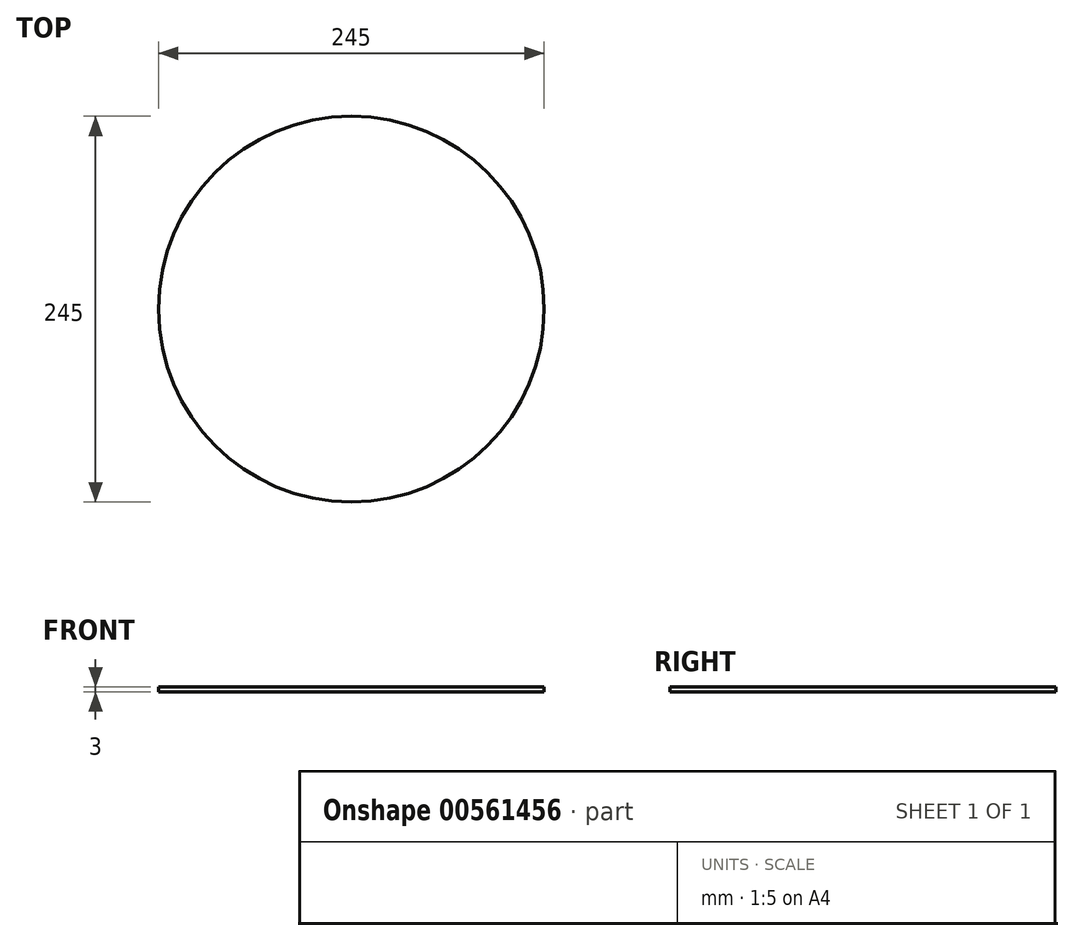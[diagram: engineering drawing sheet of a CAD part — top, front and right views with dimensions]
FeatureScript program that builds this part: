
annotation { "Feature Type Name" : "Feature", "Feature Type Description" : "" }
export const myFeature = defineFeature(function(context is Context, id is Id, definition is map)
    precondition{}
    {
        {
            var Q0;
            Q0=qCreatedBy(makeId("Top.planeOp"),FACE);
            var sketch = newSketch(context, id + "F0", { "sketchPlane" : qUnion([Q0])});
            skCircle(sketch, "E0", {"center": v(0, 0) * mm, "radius": 122.5 * mm});
            skSolve(sketch);
        }
        {
            var Q0;
            Q0=makeQuery(id+"F0.imprint","IMPRINT",FACE,{"disambiguationData":[TD([[makeQuery(id+"F0.imprint","IMPRINT",EDGE,{"derivedFrom":sQuery(id+"F0.wireOp",EDGE,"E0")}),1.0]])]});
            extrude(context, id + "F1", {"entities" : qUnion([Q0]), "depth" : 3 * mm, "offsetDistance" : 25 * mm});
        }
    });
